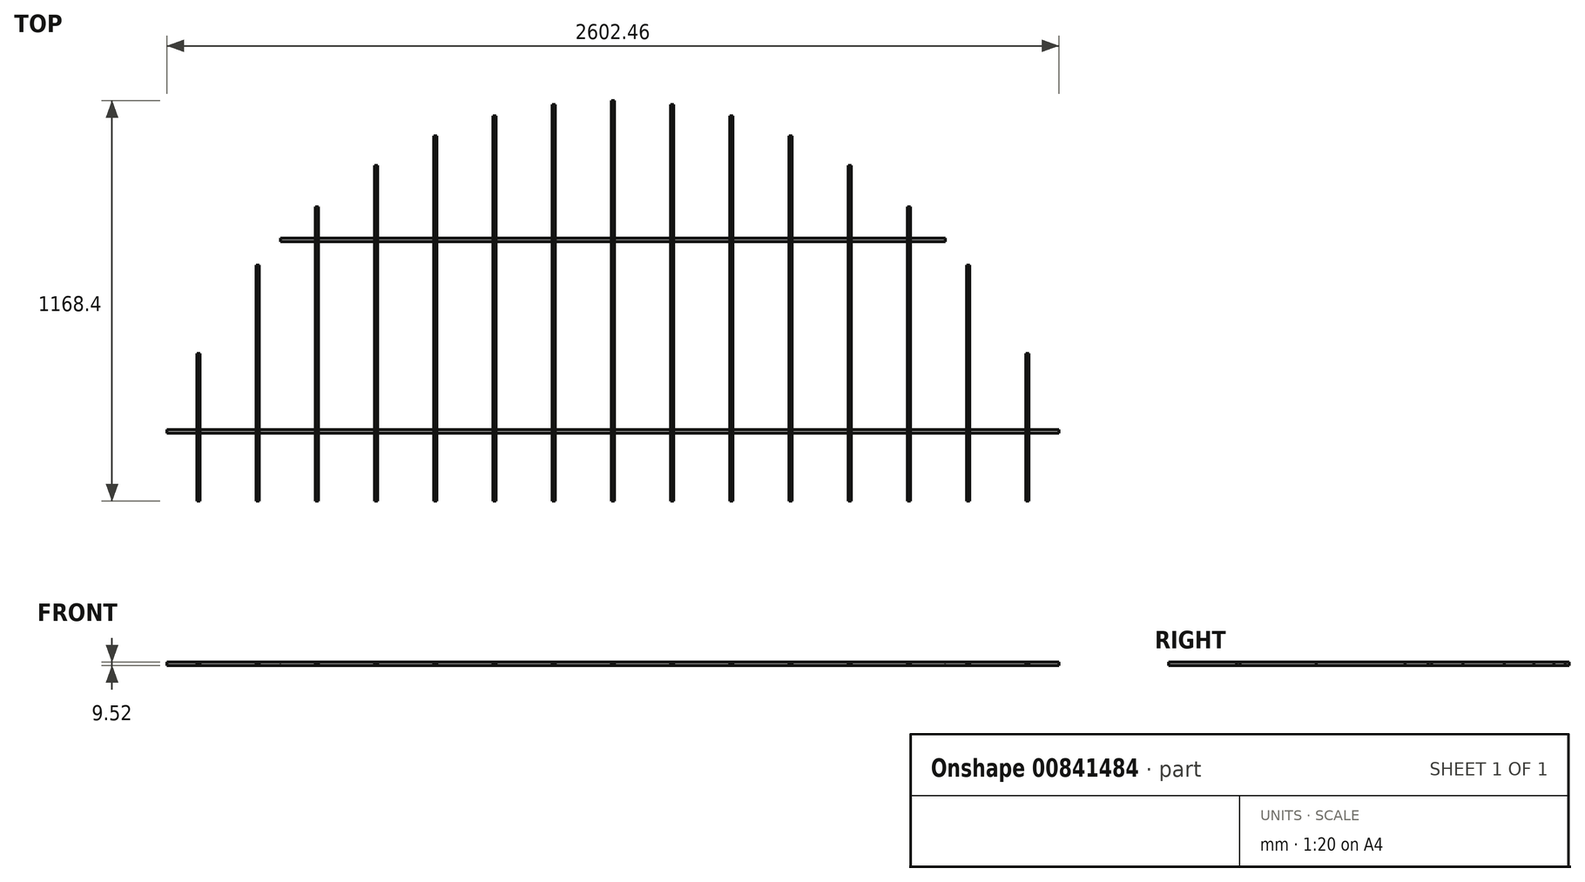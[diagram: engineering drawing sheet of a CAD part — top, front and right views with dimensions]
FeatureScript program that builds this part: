
annotation { "Feature Type Name" : "Feature", "Feature Type Description" : "" }
export const myFeature = defineFeature(function(context is Context, id is Id, definition is map)
    precondition{}
    {
        {
            var Q0;
            Q0=qCreatedBy(makeId("Top.planeOp"),FACE);
            var sketch = newSketch(context, id + "F0", { "sketchPlane" : qUnion([Q0])});
            skArc(sketch, "E0", {"start": v(1346.2, 0) * mm, "mid": v(0, 1168.4) * mm, "end": v(-1346.2, 0) * mm});
            skLineSegment(sketch, "E1", {"start": v(0, 0) * mm, "end": v(0, 1168.4) * mm});
            skLineSegment(sketch, "E2.1.0.0", {"start": v(172.72, 0) * mm, "end": v(172.72, 1157.39) * mm});
            skLineSegment(sketch, "E2.2.0.0", {"start": v(345.44, 0) * mm, "end": v(345.44, 1123.79) * mm});
            skLineSegment(sketch, "E2.3.0.0", {"start": v(518.16, 0) * mm, "end": v(518.16, 1065.8) * mm});
            skLineSegment(sketch, "E2.4.0.0", {"start": v(690.88, 0) * mm, "end": v(690.88, 979.8) * mm});
            skLineSegment(sketch, "E2.5.0.0", {"start": v(863.6, 0) * mm, "end": v(863.6, 858.94) * mm});
            skLineSegment(sketch, "E2.6.0.0", {"start": v(1036.32, 0) * mm, "end": v(1036.32, 688.96) * mm});
            skLineSegment(sketch, "E2.7.0.0", {"start": v(1209.04, 0) * mm, "end": v(1209.04, 430.83) * mm});
            skLineSegment(sketch, "E2.direction1", {"start": v(0, 0) * mm, "end": v(172.72, 0) * mm, "construction": true});
            skLineSegment(sketch, "E3.1.0.0", {"start": v(-172.72, 0) * mm, "end": v(-172.72, 1157.39) * mm});
            skLineSegment(sketch, "E3.1.0.1", {"start": v(-172.72, 0) * mm, "end": v(0, 0) * mm, "construction": true});
            skLineSegment(sketch, "E3.2.0.0", {"start": v(-345.44, 0) * mm, "end": v(-345.44, 1123.79) * mm});
            skLineSegment(sketch, "E3.3.0.0", {"start": v(-518.16, 0) * mm, "end": v(-518.16, 1065.8) * mm});
            skLineSegment(sketch, "E3.4.0.0", {"start": v(-690.88, 0) * mm, "end": v(-690.88, 979.8) * mm});
            skLineSegment(sketch, "E3.5.0.0", {"start": v(-863.6, 0) * mm, "end": v(-863.6, 858.94) * mm});
            skLineSegment(sketch, "E3.6.0.0", {"start": v(-1036.32, 0) * mm, "end": v(-1036.32, 688.96) * mm});
            skLineSegment(sketch, "E3.7.0.0", {"start": v(-1209.04, 0) * mm, "end": v(-1209.04, 430.83) * mm});
            skLineSegment(sketch, "E3.direction1", {"start": v(0, 0) * mm, "end": v(-172.72, 0) * mm, "construction": true});
            skPoint(sketch, "E4.orphan", {"position": v(-1209.04, 1168.4) * mm});
            skPoint(sketch, "E5.orphan", {"position": v(-1036.32, 1168.4) * mm});
            skPoint(sketch, "E6.orphan", {"position": v(-863.6, 1168.4) * mm});
            skPoint(sketch, "E7.orphan", {"position": v(-690.88, 1168.4) * mm});
            skPoint(sketch, "E8.orphan", {"position": v(-518.16, 1168.4) * mm});
            skPoint(sketch, "E9.orphan", {"position": v(-345.44, 1168.4) * mm});
            skPoint(sketch, "E10.orphan", {"position": v(-172.72, 1168.4) * mm});
            skPoint(sketch, "E11.orphan", {"position": v(172.72, 1168.4) * mm});
            skPoint(sketch, "E12.orphan", {"position": v(345.44, 1168.4) * mm});
            skPoint(sketch, "E13.orphan", {"position": v(518.16, 1168.4) * mm});
            skPoint(sketch, "E14.orphan", {"position": v(690.88, 1168.4) * mm});
            skPoint(sketch, "E15.orphan", {"position": v(1209.04, 1168.4) * mm});
            skPoint(sketch, "E16.orphan", {"position": v(1036.32, 1168.4) * mm});
            skPoint(sketch, "E17.orphan", {"position": v(863.6, 1168.4) * mm});
            skSolve(sketch);
        }
        {
            var Q0;
            Q0=qCreatedBy(makeId("Top.planeOp"),FACE);
            var sketch = newSketch(context, id + "F1", { "sketchPlane" : qUnion([Q0])});
            skLineSegment(sketch, "E18", {"start": v(-1301.23, 203.2) * mm, "end": v(1301.23, 203.2) * mm});
            skLineSegment(sketch, "E19", {"start": v(-969.55, 762) * mm, "end": v(969.55, 762) * mm});
            skSolve(sketch);
        }
        {
            var Q0;
            Q0=qCreatedBy(makeId("Front.planeOp"),FACE);
            var sketch = newSketch(context, id + "F2", { "sketchPlane" : qUnion([Q0])});
            skCircle(sketch, "E20", {"center": v(-1209.04, 0) * mm, "radius": 4.76 * mm});
            skCircle(sketch, "E21.1.0.0", {"center": v(-1036.32, 0) * mm, "radius": 4.76 * mm});
            skCircle(sketch, "E21.2.0.0", {"center": v(-863.6, 0) * mm, "radius": 4.76 * mm});
            skCircle(sketch, "E21.3.0.0", {"center": v(-690.88, 0) * mm, "radius": 4.76 * mm});
            skCircle(sketch, "E21.4.0.0", {"center": v(-518.16, 0) * mm, "radius": 4.76 * mm});
            skCircle(sketch, "E21.5.0.0", {"center": v(-345.44, 0) * mm, "radius": 4.76 * mm});
            skCircle(sketch, "E21.6.0.0", {"center": v(-172.72, 0) * mm, "radius": 4.76 * mm});
            skCircle(sketch, "E21.7.0.0", {"center": v(0, 0) * mm, "radius": 4.76 * mm});
            skCircle(sketch, "E21.8.0.0", {"center": v(172.72, 0) * mm, "radius": 4.76 * mm});
            skCircle(sketch, "E21.9.0.0", {"center": v(345.44, 0) * mm, "radius": 4.76 * mm});
            skCircle(sketch, "E21.10.0.0", {"center": v(518.16, 0) * mm, "radius": 4.76 * mm});
            skCircle(sketch, "E21.11.0.0", {"center": v(690.88, 0) * mm, "radius": 4.76 * mm});
            skCircle(sketch, "E21.12.0.0", {"center": v(863.6, 0) * mm, "radius": 4.76 * mm});
            skCircle(sketch, "E21.13.0.0", {"center": v(1036.32, 0) * mm, "radius": 4.76 * mm});
            skCircle(sketch, "E21.14.0.0", {"center": v(1209.04, 0) * mm, "radius": 4.76 * mm});
            skLineSegment(sketch, "E21.direction1", {"start": v(-1209.04, 0) * mm, "end": v(-1036.32, 0) * mm, "construction": true});
            skSolve(sketch);
        }
        {
            var Q0;
            Q0=makeQuery(id+"F2.imprint","IMPRINT",FACE,{"disambiguationData":[TD([[makeQuery(id+"F2.imprint","IMPRINT",EDGE,{"derivedFrom":sQuery(id+"F2.wireOp",EDGE,"E20")}),1.0]])]});
            var Q1;
            Q1=sQuery(id+"F0.wireOp",EDGE,"E3.7.0.0");
            sweep(context, id + "F3", {"profiles" : qUnion([Q0]), "path" : qUnion([Q1])});
        }
        {
            var Q0;
            Q0=makeQuery(id+"F2.imprint","IMPRINT",FACE,{"disambiguationData":[TD([[makeQuery(id+"F2.imprint","IMPRINT",EDGE,{"derivedFrom":sQuery(id+"F2.wireOp",EDGE,"E21.1.0.0")}),1.0]])]});
            var Q1;
            Q1=sQuery(id+"F0.wireOp",EDGE,"E3.6.0.0");
            sweep(context, id + "F4", {"profiles" : qUnion([Q0]), "path" : qUnion([Q1])});
        }
        {
            var Q0;
            Q0=makeQuery(id+"F2.imprint","IMPRINT",FACE,{"disambiguationData":[TD([[makeQuery(id+"F2.imprint","IMPRINT",EDGE,{"derivedFrom":sQuery(id+"F2.wireOp",EDGE,"E21.2.0.0")}),1.0]])]});
            var Q1;
            Q1=sQuery(id+"F0.wireOp",EDGE,"E3.5.0.0");
            sweep(context, id + "F5", {"profiles" : qUnion([Q0]), "path" : qUnion([Q1])});
        }
        {
            var Q0;
            Q0=makeQuery(id+"F2.imprint","IMPRINT",FACE,{"disambiguationData":[TD([[makeQuery(id+"F2.imprint","IMPRINT",EDGE,{"derivedFrom":sQuery(id+"F2.wireOp",EDGE,"E21.3.0.0")}),1.0]])]});
            var Q1;
            Q1=sQuery(id+"F0.wireOp",EDGE,"E3.4.0.0");
            sweep(context, id + "F6", {"profiles" : qUnion([Q0]), "path" : qUnion([Q1])});
        }
        {
            var Q0;
            Q0=makeQuery(id+"F2.imprint","IMPRINT",FACE,{"disambiguationData":[TD([[makeQuery(id+"F2.imprint","IMPRINT",EDGE,{"derivedFrom":sQuery(id+"F2.wireOp",EDGE,"E21.4.0.0")}),1.0]])]});
            var Q1;
            Q1=sQuery(id+"F0.wireOp",EDGE,"E3.3.0.0");
            sweep(context, id + "F7", {"profiles" : qUnion([Q0]), "path" : qUnion([Q1])});
        }
        {
            var Q0;
            Q0=makeQuery(id+"F2.imprint","IMPRINT",FACE,{"disambiguationData":[TD([[makeQuery(id+"F2.imprint","IMPRINT",EDGE,{"derivedFrom":sQuery(id+"F2.wireOp",EDGE,"E21.5.0.0")}),1.0]])]});
            var Q1;
            Q1=sQuery(id+"F0.wireOp",EDGE,"E3.2.0.0");
            sweep(context, id + "F8", {"profiles" : qUnion([Q0]), "path" : qUnion([Q1])});
        }
        {
            var Q0;
            Q0=makeQuery(id+"F2.imprint","IMPRINT",FACE,{"disambiguationData":[TD([[makeQuery(id+"F2.imprint","IMPRINT",EDGE,{"derivedFrom":sQuery(id+"F2.wireOp",EDGE,"E21.6.0.0")}),1.0]])]});
            var Q1;
            Q1=sQuery(id+"F0.wireOp",EDGE,"E3.1.0.0");
            sweep(context, id + "F9", {"profiles" : qUnion([Q0]), "path" : qUnion([Q1])});
        }
        {
            var Q0;
            Q0=makeQuery(id+"F2.imprint","IMPRINT",FACE,{"disambiguationData":[TD([[makeQuery(id+"F2.imprint","IMPRINT",EDGE,{"derivedFrom":sQuery(id+"F2.wireOp",EDGE,"E21.7.0.0")}),1.0]])]});
            var Q1;
            Q1=sQuery(id+"F0.wireOp",EDGE,"E1");
            sweep(context, id + "F10", {"profiles" : qUnion([Q0]), "path" : qUnion([Q1])});
        }
        {
            var Q0;
            Q0=makeQuery(id+"F2.imprint","IMPRINT",FACE,{"disambiguationData":[TD([[makeQuery(id+"F2.imprint","IMPRINT",EDGE,{"derivedFrom":sQuery(id+"F2.wireOp",EDGE,"E21.8.0.0")}),1.0]])]});
            var Q1;
            Q1=sQuery(id+"F0.wireOp",EDGE,"E2.1.0.0");
            sweep(context, id + "F11", {"profiles" : qUnion([Q0]), "path" : qUnion([Q1])});
        }
        {
            var Q0;
            Q0=makeQuery(id+"F2.imprint","IMPRINT",FACE,{"disambiguationData":[TD([[makeQuery(id+"F2.imprint","IMPRINT",EDGE,{"derivedFrom":sQuery(id+"F2.wireOp",EDGE,"E21.9.0.0")}),1.0]])]});
            var Q1;
            Q1=sQuery(id+"F0.wireOp",EDGE,"E2.2.0.0");
            sweep(context, id + "F12", {"profiles" : qUnion([Q0]), "path" : qUnion([Q1])});
        }
        {
            var Q0;
            Q0=makeQuery(id+"F2.imprint","IMPRINT",FACE,{"disambiguationData":[TD([[makeQuery(id+"F2.imprint","IMPRINT",EDGE,{"derivedFrom":sQuery(id+"F2.wireOp",EDGE,"E21.10.0.0")}),1.0]])]});
            var Q1;
            Q1=sQuery(id+"F0.wireOp",EDGE,"E2.3.0.0");
            sweep(context, id + "F13", {"profiles" : qUnion([Q0]), "path" : qUnion([Q1])});
        }
        {
            var Q0;
            Q0=makeQuery(id+"F2.imprint","IMPRINT",FACE,{"disambiguationData":[TD([[makeQuery(id+"F2.imprint","IMPRINT",EDGE,{"derivedFrom":sQuery(id+"F2.wireOp",EDGE,"E21.11.0.0")}),1.0]])]});
            var Q1;
            Q1=sQuery(id+"F0.wireOp",EDGE,"E2.4.0.0");
            sweep(context, id + "F14", {"profiles" : qUnion([Q0]), "path" : qUnion([Q1])});
        }
        {
            var Q0;
            Q0=makeQuery(id+"F2.imprint","IMPRINT",FACE,{"disambiguationData":[TD([[makeQuery(id+"F2.imprint","IMPRINT",EDGE,{"derivedFrom":sQuery(id+"F2.wireOp",EDGE,"E21.12.0.0")}),1.0]])]});
            var Q1;
            Q1=sQuery(id+"F0.wireOp",EDGE,"E2.5.0.0");
            sweep(context, id + "F15", {"profiles" : qUnion([Q0]), "path" : qUnion([Q1])});
        }
        {
            var Q0;
            Q0=makeQuery(id+"F2.imprint","IMPRINT",FACE,{"disambiguationData":[TD([[makeQuery(id+"F2.imprint","IMPRINT",EDGE,{"derivedFrom":sQuery(id+"F2.wireOp",EDGE,"E21.13.0.0")}),1.0]])]});
            var Q1;
            Q1=sQuery(id+"F0.wireOp",EDGE,"E2.6.0.0");
            sweep(context, id + "F16", {"profiles" : qUnion([Q0]), "path" : qUnion([Q1])});
        }
        {
            var Q0;
            Q0=makeQuery(id+"F2.imprint","IMPRINT",FACE,{"disambiguationData":[TD([[makeQuery(id+"F2.imprint","IMPRINT",EDGE,{"derivedFrom":sQuery(id+"F2.wireOp",EDGE,"E21.14.0.0")}),1.0]])]});
            var Q1;
            Q1=sQuery(id+"F0.wireOp",EDGE,"E2.7.0.0");
            sweep(context, id + "F17", {"profiles" : qUnion([Q0]), "path" : qUnion([Q1])});
        }
        {
            var Q0;
            Q0=qCreatedBy(makeId("Right.planeOp"),FACE);
            var sketch = newSketch(context, id + "F18", { "sketchPlane" : qUnion([Q0])});
            skCircle(sketch, "E22", {"center": v(762, 0) * mm, "radius": 4.76 * mm});
            skCircle(sketch, "E23", {"center": v(203.2, 0) * mm, "radius": 4.76 * mm});
            skSolve(sketch);
        }
        {
            var Q0;
            Q0=makeQuery(id+"F18.imprint","IMPRINT",FACE,{"disambiguationData":[TD([[makeQuery(id+"F18.imprint","IMPRINT",EDGE,{"derivedFrom":sQuery(id+"F18.wireOp",EDGE,"E22")}),1.0]])]});
            var Q1;
            Q1=sQuery(id+"F1.wireOp",EDGE,"E19");
            sweep(context, id + "F19", {"profiles" : qUnion([Q0]), "path" : qUnion([Q1])});
        }
        {
            var Q0;
            Q0=makeQuery(id+"F18.imprint","IMPRINT",FACE,{"disambiguationData":[TD([[makeQuery(id+"F18.imprint","IMPRINT",EDGE,{"derivedFrom":sQuery(id+"F18.wireOp",EDGE,"E23")}),1.0]])]});
            var Q1;
            Q1=sQuery(id+"F1.wireOp",EDGE,"E18");
            sweep(context, id + "F20", {"profiles" : qUnion([Q0]), "path" : qUnion([Q1])});
        }
    });
